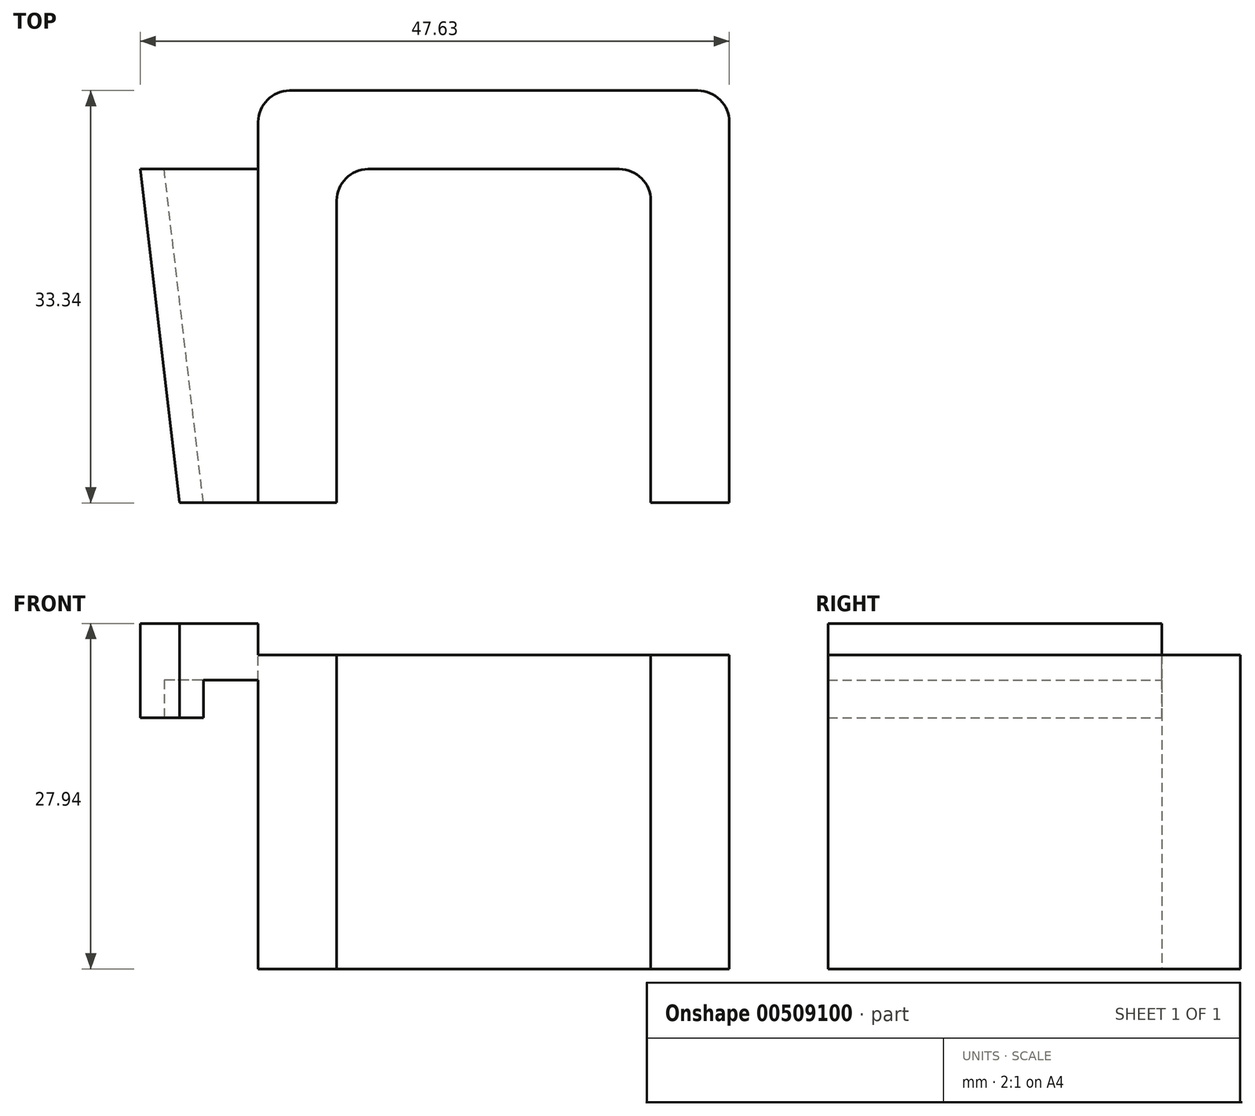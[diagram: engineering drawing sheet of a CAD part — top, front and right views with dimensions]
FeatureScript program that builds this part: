
annotation { "Feature Type Name" : "Feature", "Feature Type Description" : "" }
export const myFeature = defineFeature(function(context is Context, id is Id, definition is map)
    precondition{}
    {
        {
            var Q0;
            Q0=qCreatedBy(makeId("Top.planeOp"),FACE);
            var sketch = newSketch(context, id + "F0", { "sketchPlane" : qUnion([Q0])});
            skLineSegment(sketch, "E0", {"start": v(-27.44, 0) * mm, "end": v(35.83, 0) * mm, "construction": true});
            skLineSegment(sketch, "E1.bottom", {"start": v(31.75, -19.05) * mm, "end": v(6.35, -19.05) * mm});
            skLineSegment(sketch, "E1.top", {"start": v(31.75, -46.04) * mm, "end": v(6.35, -46.04) * mm, "construction": true});
            skLineSegment(sketch, "E1.left", {"start": v(31.75, -19.05) * mm, "end": v(31.75, -46.04) * mm});
            skLineSegment(sketch, "E1.right", {"start": v(6.35, -19.05) * mm, "end": v(6.35, -46.04) * mm});
            skPoint(sketch, "E1.middle", {"position": v(19.05, -32.54) * mm});
            skLineSegment(sketch, "E2", {"start": v(31.75, -46.04) * mm, "end": v(38.1, -46.04) * mm});
            skLineSegment(sketch, "E3", {"start": v(38.1, -46.04) * mm, "end": v(38.1, -12.7) * mm});
            skLineSegment(sketch, "E4", {"start": v(38.1, -12.7) * mm, "end": v(0, -12.7) * mm});
            skLineSegment(sketch, "E5", {"start": v(6.35, -46.04) * mm, "end": v(0, -46.04) * mm});
            skLineSegment(sketch, "E6", {"start": v(0, -46.04) * mm, "end": v(0, -12.7) * mm});
            skSolve(sketch);
        }
        {
            var Q0;
            Q0=makeQuery(id+"F0.imprint","IMPRINT",FACE,{"disambiguationData":[TD([[makeQuery(id+"F0.imprint","IMPRINT",EDGE,{"derivedFrom":sQuery(id+"F0.wireOp",EDGE,"E1.bottom")}),-1.0]])]});
            extrude(context, id + "F1", {"entities" : qUnion([Q0]), "depth" : 25.4 * mm});
        }
        {
            var Q0;
            Q0=makeQuery(id+"F1.opExtrude","CAP_FACE",FACE,{"disambiguationData":[OSD([sQuery(id+"F0.wireOp",EDGE,"E1.bottom"),sQuery(id+"F0.wireOp",EDGE,"E1.left"),sQuery(id+"F0.wireOp",EDGE,"E1.right"),sQuery(id+"F0.wireOp",EDGE,"E2"),sQuery(id+"F0.wireOp",EDGE,"E3"),sQuery(id+"F0.wireOp",EDGE,"E4"),sQuery(id+"F0.wireOp",EDGE,"E5"),sQuery(id+"F0.wireOp",EDGE,"E6")])],"isStart":false});
            var sketch = newSketch(context, id + "F2", { "sketchPlane" : qUnion([Q0])});
            skLineSegment(sketch, "E7", {"start": v(0, -19.05) * mm, "end": v(-9.53, -19.05) * mm});
            skLineSegment(sketch, "E8", {"start": v(-9.53, -19.05) * mm, "end": v(-6.35, -46.04) * mm});
            skLineSegment(sketch, "E9", {"start": v(-6.35, -46.04) * mm, "end": v(0, -46.04) * mm});
            skLineSegment(sketch, "E10", {"start": v(0, -19.05) * mm, "end": v(0, -46.04) * mm});
            skSolve(sketch);
        }
        {
            var Q0;
            Q0 = qSketchRegion(id + "F2", true);
            extrude(context, id + "F3", {"entities" : qUnion([Q0]), "operationType" : NewBodyOperationType.ADD, "oppositeDirection" : true, "depth" : 5.08 * mm, "hasSecondDirection" : true, "secondDirectionOppositeDirection" : false, "secondDirectionDepth" : 2.54 * mm});
        }
        {
            var Q0;
            Q0=makeQuery(id+"F1.opExtrude","SWEPT_EDGE",EDGE,{"disambiguationData":[OSD([sQuery(id+"F0.wireOp",EDGE,"E1.bottom"),sQuery(id+"F0.wireOp",EDGE,"E1.right")])]});
            var Q1;
            Q1=makeQuery(id+"F1.opExtrude","SWEPT_EDGE",EDGE,{"disambiguationData":[OSD([sQuery(id+"F0.wireOp",EDGE,"E1.bottom"),sQuery(id+"F0.wireOp",EDGE,"E1.left")])]});
            var Q2;
            Q2=makeQuery(id+"F1.opExtrude","SWEPT_EDGE",EDGE,{"disambiguationData":[OSD([sQuery(id+"F0.wireOp",EDGE,"E3"),sQuery(id+"F0.wireOp",EDGE,"E4")])]});
            var Q3;
            Q3=makeQuery(id+"F1.opExtrude","SWEPT_EDGE",EDGE,{"disambiguationData":[OSD([sQuery(id+"F0.wireOp",EDGE,"E4"),sQuery(id+"F0.wireOp",EDGE,"E6")])]});
            fillet(context, id + "F4", {"entities" : qUnion([Q0, Q1, Q2, Q3]), "radius" : 2.54 * mm, "tangentPropagation" : true, "allowEdgeOverflow" : false});
        }
        {
            var Q0;
            Q0=makeQuery(id+"F3.opExtrude","CAP_FACE",FACE,{"disambiguationData":[OSD([sQuery(id+"F2.wireOp",EDGE,"E7"),sQuery(id+"F2.wireOp",EDGE,"E8"),sQuery(id+"F2.wireOp",EDGE,"E9"),sQuery(id+"F2.wireOp",EDGE,"E10")])],"isStart":false});
            var sketch = newSketch(context, id + "F5", { "sketchPlane" : qUnion([Q0])});
            skLineSegment(sketch, "E11", {"start": v(-4.43, 46.04) * mm, "end": v(-7.6, 19.05) * mm});
            skLineSegment(sketch, "E12", {"start": v(-4.43, 46.04) * mm, "end": v(0, 46.04) * mm});
            skLineSegment(sketch, "E13", {"start": v(0, 46.04) * mm, "end": v(0, 19.05) * mm});
            skLineSegment(sketch, "E14", {"start": v(0, 19.05) * mm, "end": v(-7.6, 19.05) * mm});
            skSolve(sketch);
        }
        {
            var Q0;
            Q0=makeQuery(id+"F5.imprint","IMPRINT",FACE,{"disambiguationData":[TD([[makeQuery(id+"F5.imprint","IMPRINT",EDGE,{"derivedFrom":sQuery(id+"F5.wireOp",EDGE,"E11")}),1.0]])]});
            extrude(context, id + "F6", {"entities" : qUnion([Q0]), "operationType" : NewBodyOperationType.REMOVE, "oppositeDirection" : true, "depth" : 3.05 * mm});
        }
    });
